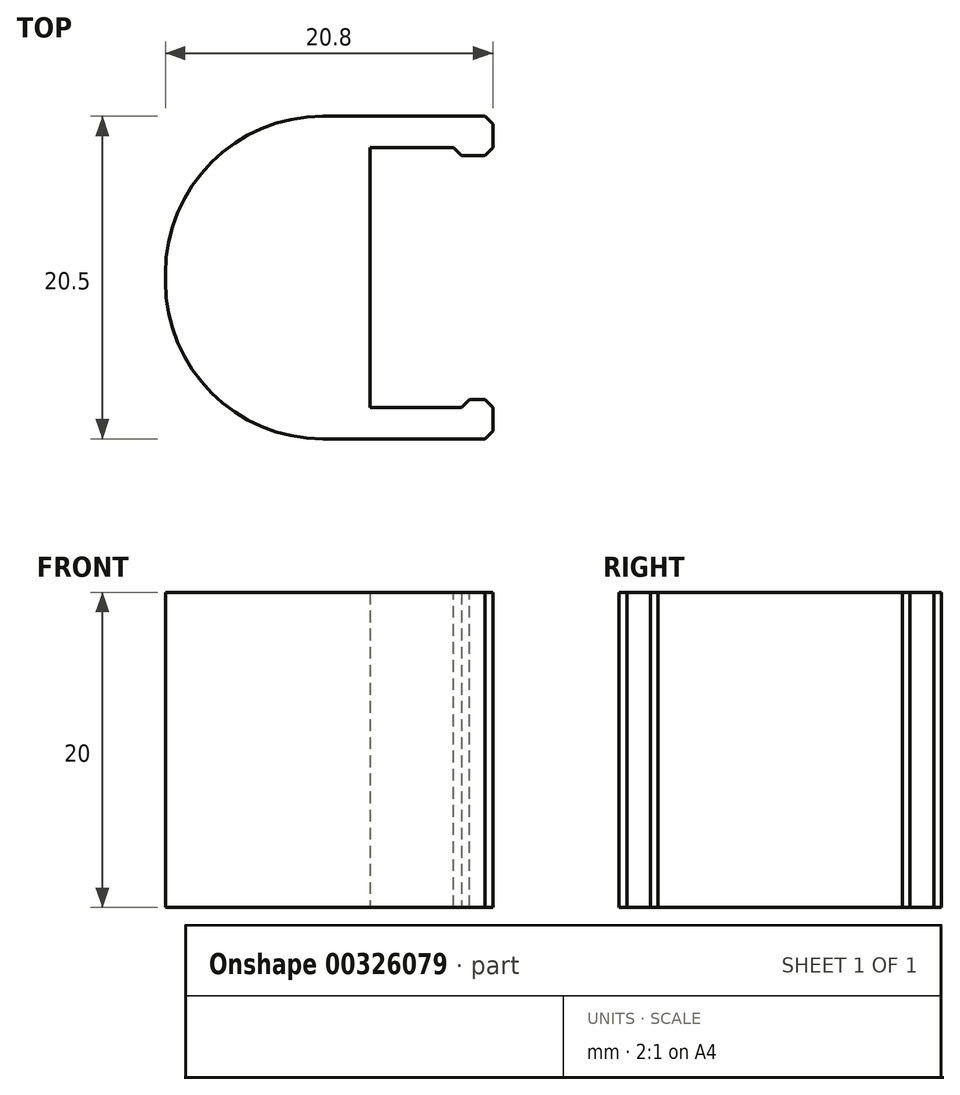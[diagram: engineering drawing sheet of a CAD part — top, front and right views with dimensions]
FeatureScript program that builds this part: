
annotation { "Feature Type Name" : "Feature", "Feature Type Description" : "" }
export const myFeature = defineFeature(function(context is Context, id is Id, definition is map)
    precondition{}
    {
        {
            var Q0;
            Q0=qCreatedBy(makeId("Top.planeOp"),FACE);
            var sketch = newSketch(context, id + "F0", { "sketchPlane" : qUnion([Q0])});
            skLineSegment(sketch, "E0.bottom", {"start": v(-54.8, 47.35) * mm, "end": v(-49, 47.35) * mm});
            skLineSegment(sketch, "E0.top", {"start": v(-54.8, 45.35) * mm, "end": v(-49, 45.35) * mm});
            skLineSegment(sketch, "E0.left", {"start": v(-54.8, 47.35) * mm, "end": v(-54.8, 45.35) * mm});
            skLineSegment(sketch, "E0.right", {"start": v(-49, 47.35) * mm, "end": v(-49, 45.35) * mm});
            skLineSegment(sketch, "E1.bottom", {"start": v(-54.8, 28.85) * mm, "end": v(-49, 28.85) * mm});
            skLineSegment(sketch, "E1.top", {"start": v(-54.8, 26.85) * mm, "end": v(-49, 26.85) * mm});
            skLineSegment(sketch, "E1.left", {"start": v(-54.8, 28.85) * mm, "end": v(-54.8, 26.85) * mm});
            skLineSegment(sketch, "E1.right", {"start": v(-49, 28.85) * mm, "end": v(-49, 26.85) * mm});
            skLineSegment(sketch, "E2.bottom", {"start": v(-54.8, 47.35) * mm, "end": v(-67.8, 47.35) * mm});
            skLineSegment(sketch, "E2.top", {"start": v(-54.8, 26.85) * mm, "end": v(-67.8, 26.85) * mm});
            skLineSegment(sketch, "E2.left", {"start": v(-54.8, 47.35) * mm, "end": v(-54.8, 26.85) * mm});
            skLineSegment(sketch, "E2.right", {"start": v(-67.8, 47.35) * mm, "end": v(-67.8, 26.85) * mm});
            skLineSegment(sketch, "E3.bottom", {"start": v(-49, 47.35) * mm, "end": v(-47, 47.35) * mm});
            skLineSegment(sketch, "E3.top", {"start": v(-49, 44.85) * mm, "end": v(-47, 44.85) * mm});
            skLineSegment(sketch, "E3.left", {"start": v(-49, 47.35) * mm, "end": v(-49, 44.85) * mm});
            skLineSegment(sketch, "E3.right", {"start": v(-47, 47.35) * mm, "end": v(-47, 44.85) * mm});
            skLineSegment(sketch, "E4.bottom", {"start": v(-49, 26.85) * mm, "end": v(-47, 26.85) * mm});
            skLineSegment(sketch, "E4.top", {"start": v(-49, 29.35) * mm, "end": v(-47, 29.35) * mm});
            skLineSegment(sketch, "E4.left", {"start": v(-49, 26.85) * mm, "end": v(-49, 29.35) * mm});
            skLineSegment(sketch, "E4.right", {"start": v(-47, 26.85) * mm, "end": v(-47, 29.35) * mm});
            skSolve(sketch);
        }
        {
            var Q0;
            Q0 = qSketchRegion(id + "F0", true);
            extrude(context, id + "F1", {"entities" : qUnion([Q0]), "depth" : 20 * mm});
        }
        {
            var Q0;
            Q0=makeQuery(id+"F1.opExtrude","SWEPT_EDGE",EDGE,{"disambiguationData":[OSD([sQuery(id+"F0.wireOp",EDGE,"E2.bottom"),sQuery(id+"F0.wireOp",EDGE,"E2.right")])]});
            var Q1;
            Q1=makeQuery(id+"F1.opExtrude","SWEPT_EDGE",EDGE,{"disambiguationData":[OSD([sQuery(id+"F0.wireOp",EDGE,"E2.top"),sQuery(id+"F0.wireOp",EDGE,"E2.right")])]});
            fillet(context, id + "F2", {"entities" : qUnion([Q0, Q1]), "radius" : 10 * mm, "tangentPropagation" : true, "allowEdgeOverflow" : false});
        }
        {
            var Q0;
            Q0=makeQuery(id+"F1.opExtrude","SWEPT_EDGE",EDGE,{"disambiguationData":[OSD([sQuery(id+"F0.wireOp",EDGE,"E3.bottom"),sQuery(id+"F0.wireOp",EDGE,"E3.right")])]});
            var Q1;
            Q1=makeQuery(id+"F1.opExtrude","SWEPT_EDGE",EDGE,{"disambiguationData":[OSD([sQuery(id+"F0.wireOp",EDGE,"E3.top"),sQuery(id+"F0.wireOp",EDGE,"E3.right")])]});
            var Q2;
            Q2=makeQuery(id+"F1.opExtrude","SWEPT_EDGE",EDGE,{"disambiguationData":[OSD([sQuery(id+"F0.wireOp",EDGE,"E4.top"),sQuery(id+"F0.wireOp",EDGE,"E4.right")])]});
            var Q3;
            Q3=makeQuery(id+"F1.opExtrude","SWEPT_EDGE",EDGE,{"disambiguationData":[OSD([sQuery(id+"F0.wireOp",EDGE,"E4.bottom"),sQuery(id+"F0.wireOp",EDGE,"E4.right")])]});
            var Q4;
            Q4=makeQuery(id+"F1.opExtrude","SWEPT_EDGE",EDGE,{"disambiguationData":[OSD([sQuery(id+"F0.wireOp",EDGE,"E4.top"),sQuery(id+"F0.wireOp",EDGE,"E4.left")])]});
            var Q5;
            Q5=makeQuery(id+"F1.opExtrude","SWEPT_EDGE",EDGE,{"disambiguationData":[OSD([sQuery(id+"F0.wireOp",EDGE,"E0.top"),sQuery(id+"F0.wireOp",EDGE,"E3.left")])]});
            chamfer(context, id + "F3", {"entities" : qUnion([Q0, Q1, Q2, Q3, Q4, Q5]), "width" : .5 * mm, "tangentPropagation" : true});
        }
    });
